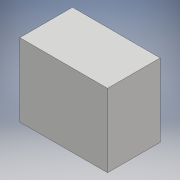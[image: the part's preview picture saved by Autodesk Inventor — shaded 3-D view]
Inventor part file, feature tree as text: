
AUTODESK INVENTOR PART (.ipt)
format: ipt  version: 2018.3 (Build 223284000, 284)  size: 85,504 bytes
history: native  units: mm
features: extrude x1, sketch x1
ambient origin geometry x8: Origin, YZ Plane, XZ Plane, XY Plane, X Axis, Y Axis, Z Axis, Center Point
bodies: Solid1 (feature_tree)
feature tree (2):
  extrude  "Extrusion1"  Depth=18.0mm
  sketch  "Sketch1"  dims[d0=30.0mm d1=18.0mm d2=25.0mm d3=0.0mm]
